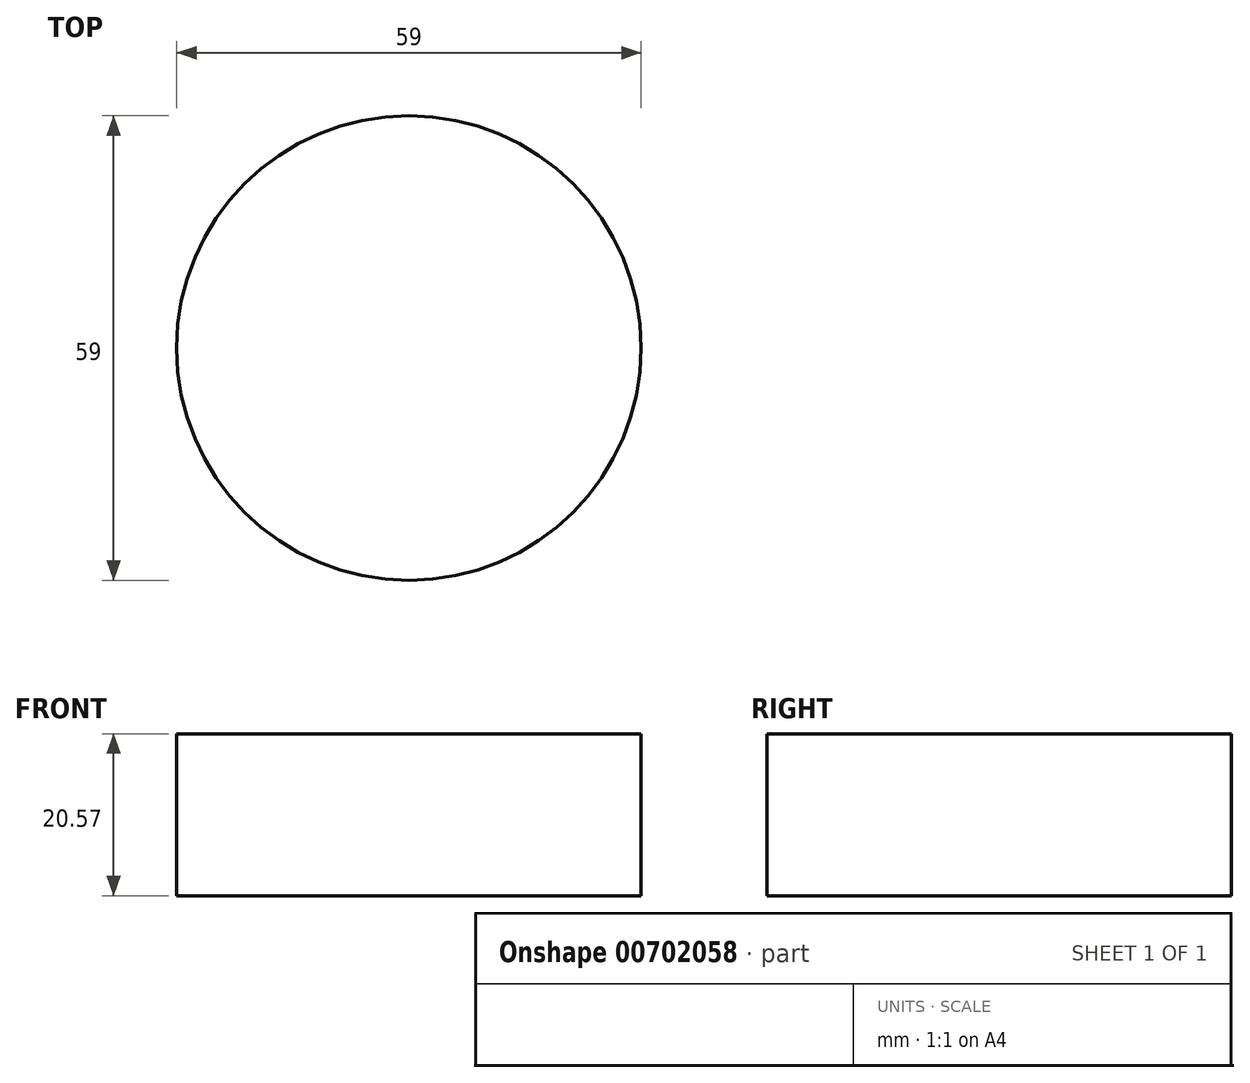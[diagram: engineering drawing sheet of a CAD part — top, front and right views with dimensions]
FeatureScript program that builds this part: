
annotation { "Feature Type Name" : "Feature", "Feature Type Description" : "" }
export const myFeature = defineFeature(function(context is Context, id is Id, definition is map)
    precondition{}
    {
        {
            var Q0;
            Q0=qCreatedBy(makeId("Top.planeOp"),FACE);
            var sketch = newSketch(context, id + "F0", { "sketchPlane" : qUnion([Q0])});
            skCircle(sketch, "E0", {"center": v(0, 0) * mm, "radius": 29.5 * mm});
            skSolve(sketch);
        }
        {
            var Q0;
            Q0=qCreatedBy(makeId("Top.planeOp"),FACE);
            cPlane(context, id + "F1", {"entities" : qUnion([Q0]), "cplaneType" : CPlaneType.OFFSET, "offset" : 20 * mm, "oppositeDirection" : true, "width" : 152.4 * mm, "height" : 152.4 * mm});
        }
        {
            var Q0;
            Q0=makeQuery(id+"F0.imprint","IMPRINT",FACE,{"disambiguationData":[TD([[makeQuery(id+"F0.imprint","IMPRINT",EDGE,{"derivedFrom":sQuery(id+"F0.wireOp",EDGE,"E0")}),1.0]])]});
            extrude(context, id + "F2", {"entities" : qUnion([Q0]), "oppositeDirection" : true, "depth" : 20.57 * mm, "offsetDistance" : 25.4 * mm});
        }
    });
